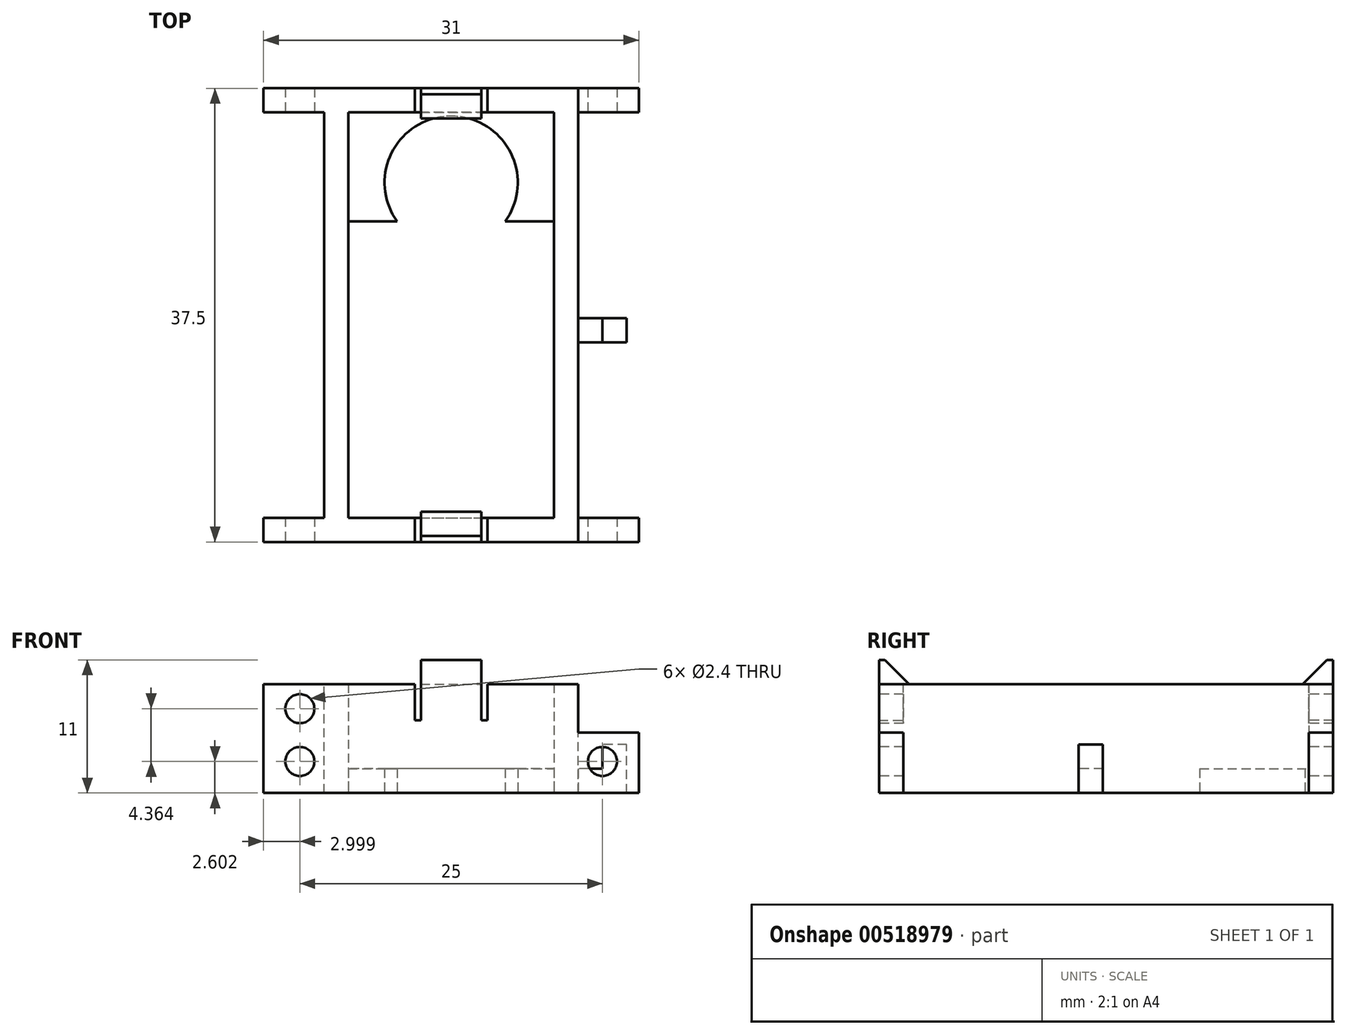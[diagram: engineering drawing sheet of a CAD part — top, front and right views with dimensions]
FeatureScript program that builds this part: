
annotation { "Feature Type Name" : "Feature", "Feature Type Description" : "" }
export const myFeature = defineFeature(function(context is Context, id is Id, definition is map)
    precondition{}
    {
        {
            var Q0;
            Q0=qCreatedBy(makeId("Top.planeOp"),FACE);
            var sketch = newSketch(context, id + "F0", { "sketchPlane" : qUnion([Q0])});
            skLineSegment(sketch, "E0.bottom", {"start": v(-9.66, 7.75) * mm, "end": v(7.34, 7.75) * mm});
            skLineSegment(sketch, "E0.top", {"start": v(-9.66, -25.75) * mm, "end": v(7.34, -25.75) * mm});
            skLineSegment(sketch, "E0.left", {"start": v(-9.66, 7.75) * mm, "end": v(-9.66, -25.75) * mm});
            skLineSegment(sketch, "E0.right", {"start": v(7.34, 7.75) * mm, "end": v(7.34, -25.75) * mm});
            skLineSegment(sketch, "E1.bottom", {"start": v(-11.66, 9.75) * mm, "end": v(9.34, 9.75) * mm});
            skLineSegment(sketch, "E1.top", {"start": v(-11.66, -27.75) * mm, "end": v(9.34, -27.75) * mm});
            skLineSegment(sketch, "E1.left", {"start": v(-11.66, 9.75) * mm, "end": v(-11.66, -27.75) * mm});
            skLineSegment(sketch, "E1.right", {"start": v(9.34, 9.75) * mm, "end": v(9.34, -27.75) * mm});
            skLineSegment(sketch, "E2", {"start": v(7.34, 0) * mm, "end": v(9.34, 0) * mm, "construction": true});
            skLineSegment(sketch, "E3", {"start": v(-9.66, 5.82) * mm, "end": v(-11.66, 5.82) * mm, "construction": true});
            skLineSegment(sketch, "E4", {"start": v(13.26, 7.75) * mm, "end": v(13.26, 9.75) * mm, "construction": true});
            skLineSegment(sketch, "E5", {"start": v(14.78, -25.75) * mm, "end": v(14.78, -27.75) * mm, "construction": true});
            skLineSegment(sketch, "E6.top", {"start": v(-9.66, -1.25) * mm, "end": v(7.34, -1.25) * mm});
            skLineSegment(sketch, "E6.left", {"start": v(-9.66, 7.75) * mm, "end": v(-9.66, -1.25) * mm});
            skLineSegment(sketch, "E6.right", {"start": v(7.34, 7.75) * mm, "end": v(7.34, -1.25) * mm});
            skLineSegment(sketch, "E7.top", {"start": v(-9.66, -16.75) * mm, "end": v(7.34, -16.75) * mm});
            skLineSegment(sketch, "E7.left", {"start": v(-9.66, -25.75) * mm, "end": v(-9.66, -16.75) * mm});
            skLineSegment(sketch, "E7.right", {"start": v(7.34, -25.75) * mm, "end": v(7.34, -16.75) * mm});
            skCircle(sketch, "E8", {"center": v(-1.16, 1.95) * mm, "radius": 5.5 * mm});
            skCircle(sketch, "E9", {"center": v(-1.16, -19.95) * mm, "radius": 5.5 * mm});
            skLineSegment(sketch, "E10", {"start": v(-1.16, 7.75) * mm, "end": v(-1.16, 1.95) * mm, "construction": true});
            skLineSegment(sketch, "E11", {"start": v(-1.16, -25.75) * mm, "end": v(-1.16, -19.95) * mm, "construction": true});
            skLineSegment(sketch, "E12.bottom", {"start": v(-5.16, 9.75) * mm, "end": v(2.84, 9.75) * mm});
            skLineSegment(sketch, "E13.bottom", {"start": v(-5.16, -27.75) * mm, "end": v(2.84, -27.75) * mm});
            skLineSegment(sketch, "E13.left", {"start": v(-5.16, -27.75) * mm, "end": v(-5.16, -35.75) * mm});
            skLineSegment(sketch, "E13.right", {"start": v(2.84, -27.75) * mm, "end": v(2.84, -35.75) * mm});
            skCircle(sketch, "E14", {"center": v(-1.16, 13.5) * mm, "radius": 1.7 * mm});
            skLineSegment(sketch, "E15", {"start": v(-1.16, -31.5) * mm, "end": v(-1.16, -27.75) * mm, "construction": true});
            skLineSegment(sketch, "E16", {"start": v(-1.16, 13.5) * mm, "end": v(-1.16, 9.75) * mm, "construction": true});
            skSolve(sketch);
        }
        {
            var Q0;
            Q0=makeQuery(id+"F0.imprint","IMPRINT",FACE,{"disambiguationData":[TD([[makeQuery(id+"F0.imprint","IMPRINT",EDGE,{"derivedFrom":sQuery(id+"F0.wireOp",EDGE,"E0.left")}),-1.0]])]});
            var Q1;
            Q1=makeQuery(id+"F0.imprint","IMPRINT",FACE,{"disambiguationData":[TD([[makeQuery(id+"F0.imprint","IMPRINT",EDGE,{"derivedFrom":sQuery(id+"F0.wireOp",EDGE,"E0.bottom")}),-1.0]])]});
            var Q2;
            Q2=makeQuery(id+"F0.imprint","IMPRINT",FACE,{"disambiguationData":[TD([[makeQuery(id+"F0.imprint","IMPRINT",EDGE,{"derivedFrom":sQuery(id+"F0.wireOp",EDGE,"E0.top")}),1.0]])]});
            var Q3;
            Q3=makeQuery(id+"F0.imprint","IMPRINT",FACE,{"disambiguationData":[TD([[makeQuery(id+"F0.imprint","IMPRINT",EDGE,{"derivedFrom":sQuery(id+"F0.wireOp",EDGE,"E12.bottom")}),1.0]])]});
            var Q4;
            Q4=makeQuery(id+"F0.imprint","IMPRINT",FACE,{"disambiguationData":[TD([[makeQuery(id+"F0.imprint","IMPRINT",EDGE,{"derivedFrom":sQuery(id+"F0.wireOp",EDGE,"E13.bottom")}),-1.0]])]});
            extrude(context, id + "F1", {"entities" : qUnion([Q0, Q1, Q2, Q3, Q4]), "depth" : 2 * mm, "offsetDistance" : 25 * mm});
        }
        {
            var Q0;
            Q0=makeQuery(id+"F0.imprint","IMPRINT",FACE,{"disambiguationData":[TD([[makeQuery(id+"F0.imprint","IMPRINT",EDGE,{"derivedFrom":sQuery(id+"F0.wireOp",EDGE,"E0.left")}),-1.0]])]});
            extrude(context, id + "F2", {"entities" : qUnion([Q0]), "operationType" : NewBodyOperationType.ADD, "depth" : 9 * mm, "offsetDistance" : 25 * mm});
        }
        {
            var Q0;
            {var subQ0=sQuery(id+"F0.wireOp",EDGE,"E1.left");Q0=makeQuery(id+"F2.boolean.opBoolean","MERGE",FACE,{"derivedFrom":[makeQuery(id+"F1.opExtrude","SWEPT_FACE",FACE,{"disambiguationData":[OSD([subQ0])]}),makeQuery(id+"F2.opExtrude","SWEPT_FACE",FACE,{"disambiguationData":[OSD([subQ0])]})]});}
            var sketch = newSketch(context, id + "F3", { "sketchPlane" : qUnion([Q0])});
            skLineSegment(sketch, "E17.bottom", {"start": v(-9.75, 0) * mm, "end": v(-7.75, 0) * mm});
            skLineSegment(sketch, "E17.top", {"start": v(-9.75, 5) * mm, "end": v(-7.75, 5) * mm});
            skLineSegment(sketch, "E17.left", {"start": v(-9.75, 0) * mm, "end": v(-9.75, 5) * mm});
            skLineSegment(sketch, "E17.right", {"start": v(-7.75, 0) * mm, "end": v(-7.75, 5) * mm});
            skLineSegment(sketch, "E18.bottom", {"start": v(27.75, 0) * mm, "end": v(25.75, 0) * mm});
            skLineSegment(sketch, "E18.top", {"start": v(27.75, 5) * mm, "end": v(25.75, 5) * mm});
            skLineSegment(sketch, "E18.left", {"start": v(27.75, 0) * mm, "end": v(27.75, 5) * mm});
            skLineSegment(sketch, "E18.right", {"start": v(25.75, 0) * mm, "end": v(25.75, 5) * mm});
            skLineSegment(sketch, "E19.bottom", {"start": v(-9.75, 9) * mm, "end": v(-7.75, 9) * mm});
            skLineSegment(sketch, "E19.left", {"start": v(-9.75, 9) * mm, "end": v(-9.75, 5) * mm});
            skLineSegment(sketch, "E19.right", {"start": v(-7.75, 9) * mm, "end": v(-7.75, 5) * mm});
            skLineSegment(sketch, "E20.bottom", {"start": v(25.75, 5) * mm, "end": v(27.75, 5) * mm});
            skLineSegment(sketch, "E20.top", {"start": v(25.75, 9) * mm, "end": v(27.75, 9) * mm});
            skLineSegment(sketch, "E20.left", {"start": v(25.75, 5) * mm, "end": v(25.75, 9) * mm});
            skLineSegment(sketch, "E20.right", {"start": v(27.75, 5) * mm, "end": v(27.75, 9) * mm});
            skSolve(sketch);
        }
        {
            var Q0;
            Q0 = qSketchRegion(id + "F3", true);
            extrude(context, id + "F4", {"entities" : qUnion([Q0]), "operationType" : NewBodyOperationType.ADD, "depth" : 5 * mm, "offsetDistance" : 25 * mm});
        }
        {
            var Q0;
            {var subQ0=sQuery(id+"F0.wireOp",EDGE,"E1.right");Q0=makeQuery(id+"F2.boolean.opBoolean","MERGE",FACE,{"derivedFrom":[makeQuery(id+"F1.opExtrude","SWEPT_FACE",FACE,{"disambiguationData":[OSD([subQ0])]}),makeQuery(id+"F2.opExtrude","SWEPT_FACE",FACE,{"disambiguationData":[OSD([subQ0])]})]});}
            var sketch = newSketch(context, id + "F5", { "sketchPlane" : qUnion([Q0])});
            skLineSegment(sketch, "E21.bottom", {"start": v(-27.75, 0) * mm, "end": v(-25.75, 0) * mm});
            skLineSegment(sketch, "E21.top", {"start": v(-27.75, 5) * mm, "end": v(-25.75, 5) * mm});
            skLineSegment(sketch, "E21.left", {"start": v(-27.75, 0) * mm, "end": v(-27.75, 5) * mm});
            skLineSegment(sketch, "E21.right", {"start": v(-25.75, 0) * mm, "end": v(-25.75, 5) * mm});
            skLineSegment(sketch, "E22.bottom", {"start": v(9.75, 0) * mm, "end": v(7.75, 0) * mm});
            skLineSegment(sketch, "E22.top", {"start": v(9.75, 5) * mm, "end": v(7.75, 5) * mm});
            skLineSegment(sketch, "E22.left", {"start": v(9.75, 0) * mm, "end": v(9.75, 5) * mm});
            skLineSegment(sketch, "E22.right", {"start": v(7.75, 0) * mm, "end": v(7.75, 5) * mm});
            skSolve(sketch);
        }
        {
            var Q0;
            Q0 = qSketchRegion(id + "F5", true);
            extrude(context, id + "F6", {"entities" : qUnion([Q0]), "operationType" : NewBodyOperationType.ADD, "depth" : 5 * mm, "offsetDistance" : 25 * mm});
        }
        {
            var Q0;
            {var subQ0=sQuery(id+"F0.wireOp",EDGE,"E13.bottom");var subQ1=sQuery(id+"F0.wireOp",EDGE,"E1.top");Q0=makeQuery(id+"F6.boolean.opBoolean","MERGE",FACE,{"derivedFrom":[makeQuery(id+"F4.boolean.opBoolean","MERGE",FACE,{"derivedFrom":[makeQuery(id+"F2.boolean.opBoolean","MERGE",FACE,{"derivedFrom":[makeQuery(id+"F1.opExtrude","SWEPT_FACE",FACE,{"disambiguationData":[OSD([subQ1,subQ0])]}),makeQuery(id+"F2.opExtrude","SWEPT_FACE",FACE,{"disambiguationData":[OSD([subQ1,subQ0])]})]}),makeQuery(id+"F4.opExtrude","SWEPT_FACE",FACE,{"disambiguationData":[OSD([sQuery(id+"F3.wireOp",EDGE,"E18.left")])]})]}),makeQuery(id+"F6.opExtrude","SWEPT_FACE",FACE,{"disambiguationData":[OSD([sQuery(id+"F5.wireOp",EDGE,"E21.left")])]})]});}
            var sketch = newSketch(context, id + "F7", { "sketchPlane" : qUnion([Q0])});
            skCircle(sketch, "E23", {"center": v(-13.66, 2.6) * mm, "radius": 1.2 * mm});
            skPoint(sketch, "E23.centerSnap0", {"position": v(-13.66, 5) * mm});
            skCircle(sketch, "E24", {"center": v(11.34, 2.6) * mm, "radius": 1.2 * mm});
            skLineSegment(sketch, "E25", {"start": v(-13.66, 2.6) * mm, "end": v(-16.66, 2.6) * mm, "construction": true});
            skLineSegment(sketch, "E26", {"start": v(11.34, 2.6) * mm, "end": v(14.34, 2.6) * mm, "construction": true});
            skCircle(sketch, "E27", {"center": v(-13.66, 6.97) * mm, "radius": 1.2 * mm});
            skSolve(sketch);
        }
        {
            var Q0;
            Q0 = qSketchRegion(id + "F7", true);
            extrude(context, id + "F8", {"entities" : qUnion([Q0]), "operationType" : NewBodyOperationType.REMOVE, "oppositeDirection" : true, "depth" : 40 * mm, "offsetDistance" : 25 * mm});
        }
        {
            var Q0;
            {var subQ0=sQuery(id+"F0.wireOp",EDGE,"E12.bottom");var subQ1=sQuery(id+"F0.wireOp",EDGE,"E1.bottom");Q0=makeQuery(id+"F6.boolean.opBoolean","MERGE",FACE,{"derivedFrom":[makeQuery(id+"F4.boolean.opBoolean","MERGE",FACE,{"derivedFrom":[makeQuery(id+"F2.boolean.opBoolean","MERGE",FACE,{"derivedFrom":[makeQuery(id+"F1.opExtrude","SWEPT_FACE",FACE,{"disambiguationData":[OSD([subQ1,subQ0])]}),makeQuery(id+"F2.opExtrude","SWEPT_FACE",FACE,{"disambiguationData":[OSD([subQ1,subQ0])]})]}),makeQuery(id+"F4.opExtrude","SWEPT_FACE",FACE,{"disambiguationData":[OSD([sQuery(id+"F3.wireOp",EDGE,"E17.left")])]})]}),makeQuery(id+"F6.opExtrude","SWEPT_FACE",FACE,{"disambiguationData":[OSD([sQuery(id+"F5.wireOp",EDGE,"E22.left")])]})]});}
            cPlane(context, id + "F9", {"entities" : qUnion([Q0]), "cplaneType" : CPlaneType.OFFSET, "offset" : 20 * mm, "oppositeDirection" : true, "width" : 150 * mm, "height" : 150 * mm});
        }
        {
            var Q0;
            Q0=qCreatedBy(id+"F9.planeOp",FACE);
            var sketch = newSketch(context, id + "F10", { "sketchPlane" : qUnion([Q0])});
            skLineSegment(sketch, "E28", {"start": v(-13.34, 0) * mm, "end": v(-13.34, 4) * mm});
            skLineSegment(sketch, "E29", {"start": v(-13.34, 4) * mm, "end": v(-11.34, 4) * mm});
            skLineSegment(sketch, "E30", {"start": v(-11.34, 4) * mm, "end": v(-11.34, 2) * mm});
            skLineSegment(sketch, "E31", {"start": v(-11.34, 2) * mm, "end": v(-9.34, 2) * mm});
            skLineSegment(sketch, "E32", {"start": v(-9.34, 2) * mm, "end": v(-9.34, 0) * mm});
            skLineSegment(sketch, "E33", {"start": v(-9.34, 0) * mm, "end": v(-13.34, 0) * mm});
            skSolve(sketch);
        }
        {
            var Q0;
            Q0 = qSketchRegion(id + "F10", true);
            extrude(context, id + "F11", {"entities" : qUnion([Q0]), "operationType" : NewBodyOperationType.ADD, "depth" : 2 * mm, "offsetDistance" : 25 * mm, "symmetric" : true});
        }
        {
            var Q0;
            Q0=makeQuery(id+"F2.opExtrude","CAP_FACE",FACE,{"disambiguationData":[OSD([sQuery(id+"F0.wireOp",EDGE,"E0.left"),sQuery(id+"F0.wireOp",EDGE,"E0.right"),sQuery(id+"F0.wireOp",EDGE,"E1.bottom"),sQuery(id+"F0.wireOp",EDGE,"E1.top"),sQuery(id+"F0.wireOp",EDGE,"E1.left"),sQuery(id+"F0.wireOp",EDGE,"E1.right"),sQuery(id+"F0.wireOp",EDGE,"E0.bottom"),sQuery(id+"F0.wireOp",EDGE,"E6.left"),sQuery(id+"F0.wireOp",EDGE,"E6.right"),sQuery(id+"F0.wireOp",EDGE,"E0.top"),sQuery(id+"F0.wireOp",EDGE,"E7.left"),sQuery(id+"F0.wireOp",EDGE,"E7.right"),sQuery(id+"F0.wireOp",EDGE,"E12.bottom"),sQuery(id+"F0.wireOp",EDGE,"E13.bottom")])],"isStart":false});
            var sketch = newSketch(context, id + "F12", { "sketchPlane" : qUnion([Q0])});
            skLineSegment(sketch, "E34.bottom", {"start": v(-3.66, 9.75) * mm, "end": v(1.34, 9.75) * mm});
            skLineSegment(sketch, "E34.top", {"start": v(-3.66, 7.25) * mm, "end": v(1.34, 7.25) * mm});
            skLineSegment(sketch, "E34.left", {"start": v(-3.66, 9.75) * mm, "end": v(-3.66, 7.25) * mm});
            skLineSegment(sketch, "E34.right", {"start": v(1.34, 9.75) * mm, "end": v(1.34, 7.25) * mm});
            skLineSegment(sketch, "E35.bottom", {"start": v(-3.66, -27.75) * mm, "end": v(1.34, -27.75) * mm});
            skLineSegment(sketch, "E35.top", {"start": v(-3.66, -25.25) * mm, "end": v(1.34, -25.25) * mm});
            skLineSegment(sketch, "E35.left", {"start": v(-3.66, -27.75) * mm, "end": v(-3.66, -25.25) * mm});
            skLineSegment(sketch, "E35.right", {"start": v(1.34, -27.75) * mm, "end": v(1.34, -25.25) * mm});
            skLineSegment(sketch, "E36", {"start": v(1.34, -25.43) * mm, "end": v(7.34, -25.43) * mm, "construction": true});
            skLineSegment(sketch, "E37", {"start": v(-3.66, -25.4) * mm, "end": v(-9.66, -25.4) * mm, "construction": true});
            skLineSegment(sketch, "E38.bottom", {"start": v(-3.66, 9.75) * mm, "end": v(-4.16, 9.75) * mm});
            skLineSegment(sketch, "E38.top", {"start": v(-3.66, 7.75) * mm, "end": v(-4.16, 7.75) * mm});
            skLineSegment(sketch, "E38.left", {"start": v(-3.66, 9.75) * mm, "end": v(-3.66, 7.75) * mm});
            skLineSegment(sketch, "E38.right", {"start": v(-4.16, 9.75) * mm, "end": v(-4.16, 7.75) * mm});
            skLineSegment(sketch, "E39.bottom", {"start": v(1.34, 9.75) * mm, "end": v(1.84, 9.75) * mm});
            skLineSegment(sketch, "E39.top", {"start": v(1.34, 7.75) * mm, "end": v(1.84, 7.75) * mm});
            skLineSegment(sketch, "E39.left", {"start": v(1.34, 9.75) * mm, "end": v(1.34, 7.75) * mm});
            skLineSegment(sketch, "E39.right", {"start": v(1.84, 9.75) * mm, "end": v(1.84, 7.75) * mm});
            skLineSegment(sketch, "E40.bottom", {"start": v(1.34, -27.75) * mm, "end": v(1.84, -27.75) * mm});
            skLineSegment(sketch, "E40.top", {"start": v(1.34, -25.75) * mm, "end": v(1.84, -25.75) * mm});
            skLineSegment(sketch, "E40.left", {"start": v(1.34, -27.75) * mm, "end": v(1.34, -25.75) * mm});
            skLineSegment(sketch, "E40.right", {"start": v(1.84, -27.75) * mm, "end": v(1.84, -25.75) * mm});
            skLineSegment(sketch, "E41.bottom", {"start": v(-3.66, -27.75) * mm, "end": v(-4.16, -27.75) * mm});
            skLineSegment(sketch, "E41.top", {"start": v(-3.66, -25.75) * mm, "end": v(-4.16, -25.75) * mm});
            skLineSegment(sketch, "E41.left", {"start": v(-3.66, -27.75) * mm, "end": v(-3.66, -25.75) * mm});
            skLineSegment(sketch, "E41.right", {"start": v(-4.16, -27.75) * mm, "end": v(-4.16, -25.75) * mm});
            skSolve(sketch);
        }
        {
            var Q0;
            Q0=makeQuery(id+"F12.imprint","IMPRINT",FACE,{"disambiguationData":[TD([[makeQuery(id+"F12.imprint","IMPRINT",EDGE,{"derivedFrom":sQuery(id+"F12.wireOp",EDGE,"E35.bottom")}),1.0]])]});
            var Q1;
            Q1=makeQuery(id+"F12.imprint","IMPRINT",FACE,{"disambiguationData":[TD([[makeQuery(id+"F12.imprint","IMPRINT",EDGE,{"derivedFrom":sQuery(id+"F12.wireOp",EDGE,"E35.top")}),-1.0]])]});
            var Q2;
            Q2=makeQuery(id+"F12.imprint","IMPRINT",FACE,{"disambiguationData":[TD([[makeQuery(id+"F12.imprint","IMPRINT",EDGE,{"derivedFrom":sQuery(id+"F12.wireOp",EDGE,"E34.bottom")}),-1.0]])]});
            var Q3;
            Q3=makeQuery(id+"F12.imprint","IMPRINT",FACE,{"disambiguationData":[TD([[makeQuery(id+"F12.imprint","IMPRINT",EDGE,{"derivedFrom":sQuery(id+"F12.wireOp",EDGE,"E34.top")}),1.0]])]});
            extrude(context, id + "F13", {"entities" : qUnion([Q0, Q1, Q2, Q3]), "operationType" : NewBodyOperationType.ADD, "depth" : 2 * mm, "offsetDistance" : 25 * mm});
        }
        {
            var Q0;
            Q0=makeQuery(id+"F13.opExtrude","CAP_EDGE",EDGE,{"disambiguationData":[OSD([sQuery(id+"F12.wireOp",EDGE,"E35.top")])],"isStart":false});
            var Q1;
            Q1=makeQuery(id+"F13.opExtrude","CAP_EDGE",EDGE,{"disambiguationData":[OSD([sQuery(id+"F12.wireOp",EDGE,"E34.top")])],"isStart":false});
            chamfer(context, id + "F14", {"entities" : qUnion([Q0, Q1]), "width" : 2 * mm, "tangentPropagation" : true});
        }
        {
            var Q0;
            Q0=makeQuery(id+"F12.imprint","IMPRINT",FACE,{"disambiguationData":[TD([[makeQuery(id+"F12.imprint","IMPRINT",EDGE,{"derivedFrom":sQuery(id+"F12.wireOp",EDGE,"E41.bottom")}),1.0]])]});
            var Q1;
            Q1=makeQuery(id+"F12.imprint","IMPRINT",FACE,{"disambiguationData":[TD([[makeQuery(id+"F12.imprint","IMPRINT",EDGE,{"derivedFrom":sQuery(id+"F12.wireOp",EDGE,"E40.bottom")}),1.0]])]});
            var Q2;
            Q2=makeQuery(id+"F12.imprint","IMPRINT",FACE,{"disambiguationData":[TD([[makeQuery(id+"F12.imprint","IMPRINT",EDGE,{"derivedFrom":sQuery(id+"F12.wireOp",EDGE,"E39.bottom")}),-1.0]])]});
            var Q3;
            Q3=makeQuery(id+"F12.imprint","IMPRINT",FACE,{"disambiguationData":[TD([[makeQuery(id+"F12.imprint","IMPRINT",EDGE,{"derivedFrom":sQuery(id+"F12.wireOp",EDGE,"E38.bottom")}),-1.0]])]});
            extrude(context, id + "F15", {"entities" : qUnion([Q0, Q1, Q2, Q3]), "operationType" : NewBodyOperationType.REMOVE, "oppositeDirection" : true, "depth" : 3 * mm, "offsetDistance" : 25 * mm});
        }
    });
